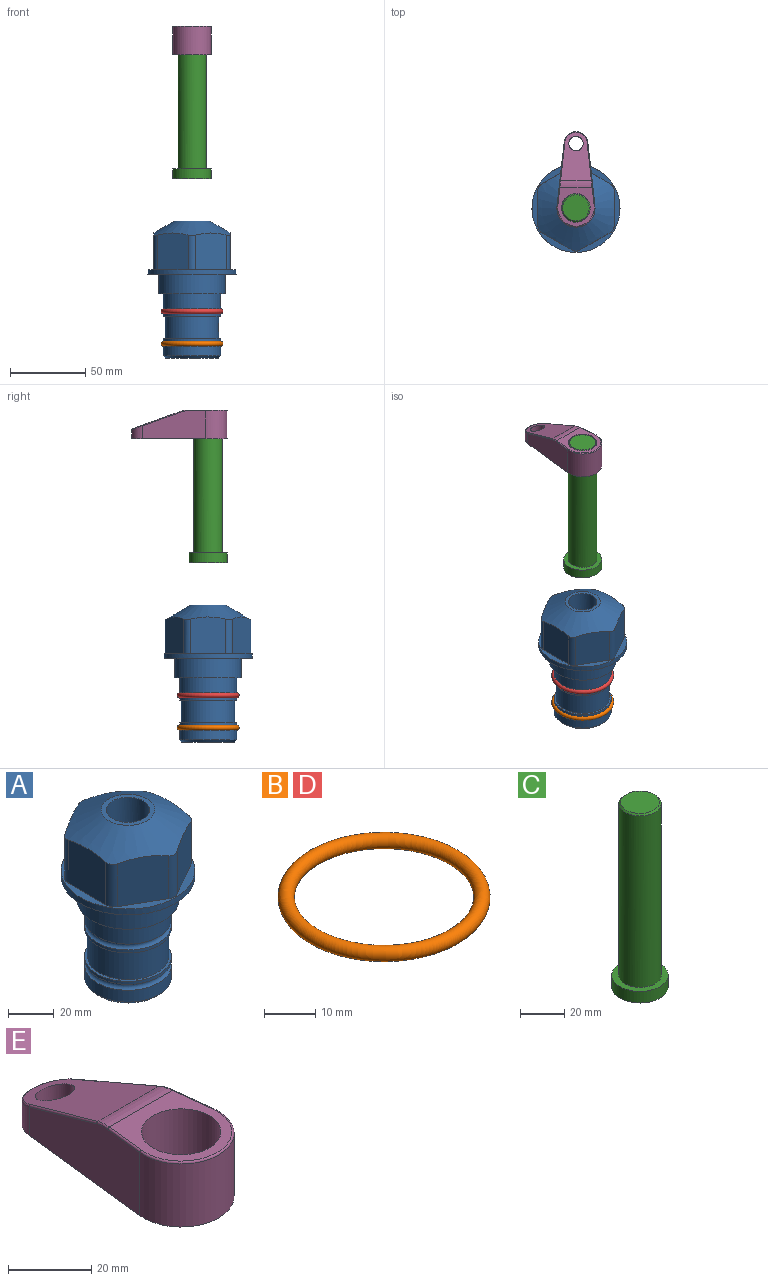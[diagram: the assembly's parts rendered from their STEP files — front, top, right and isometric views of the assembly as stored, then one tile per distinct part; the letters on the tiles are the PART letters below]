
ASSEMBLY  parts=5 mates=3
PART A: 36 faces, bbox 58.7x58.7x91.2 mm
  f0: cylinder r=17.78mm len=35.56mm, axis (0,0,1), area 1670.8mm2, adj f23,f24,f31
  f1: cylinder r=19.05mm len=38.1mm, axis (0,0,1), area 1191.9mm2, adj f26,f27,f30
  f2: plane 58.66x58.66mm, normal (0,0,-1), area 1150.6mm2, adj f3,f28
  f3: cylinder r=29.33mm len=58.66mm, axis (0,0,-1), area 585.1mm2, adj f2,f4
  f4: plane 58.66x58.66mm, normal (0,0,1), area 475.9mm2, adj f3,f5,f6,f7,f8,f9,f10,f11
  f5: plane 24.5x20.32mm, normal (-0.5,0.87,0), area 562.8mm2, adj f4,f15,f16,f17
  f6: plane 24.5x20.32mm, normal (0.5,0.87,0), area 562.8mm2, adj f4,f14,f15,f17
  f7: plane 24.5x23.48mm, normal (1,0,0), area 562.8mm2, adj f4,f13,f14,f17
  f8: plane 24.5x20.32mm, normal (0.5,-0.87,0), area 562.8mm2, adj f4,f12,f13,f17
  f9: plane 24.5x20.32mm, normal (-0.5,-0.87,0), area 562.8mm2, adj f4,f11,f12,f17
  f10: plane 24.5x23.48mm, normal (-1,0,0), area 562.8mm2, adj f4,f11,f16,f17
  f11: cylinder r=5.08mm len=23.01mm, axis (0,0,-1), area 121.2mm2, adj f4,f9,f10,f17
  f12: cylinder r=5.08mm len=23.01mm, axis (0,0,-1), area 121.2mm2, adj f4,f8,f9,f17
  f13: cylinder r=5.08mm len=23.01mm, axis (0,0,-1), area 121.2mm2, adj f4,f7,f8,f17
  f14: cylinder r=5.08mm len=23.01mm, axis (0,0,-1), area 121.2mm2, adj f4,f6,f7,f17
  f15: cylinder r=5.08mm len=23.01mm, axis (0,0,-1), area 121.2mm2, adj f4,f5,f6,f17
  f16: cylinder r=5.08mm len=23.01mm, axis (0,0,-1), area 121.2mm2, adj f4,f5,f10,f17
  f17: cone r=11.73mm half-angle=60deg, axis (0,0,-1), area 2071.8mm2, adj f5,f6,f7,f8,f9,f10,f11,f12
  f18: plane 23.46x23.46mm, normal (0,0,1), area 147.4mm2, adj f17,f35
  f19: plane 34.93x34.93mm, normal (0,0,-1), area 958mm2, adj f29
  f20: cylinder r=19.05mm len=38.1mm, axis (0,0,1), area 760.1mm2, adj f21,f29
  f21: torus R=19.05mm, axis (0,0,1), area 565.3mm2, adj f20,f22
  f22: cylinder r=19.05mm len=38.1mm, axis (0,0,1), area 190mm2, adj f21,f23
  f23: plane 38.1x38.1mm, normal (0,0,1), area 146.9mm2, adj f0,f22
  f24: plane 38.1x38.1mm, normal (0,0,-1), area 146.9mm2, adj f0,f25
  f25: cylinder r=19.05mm len=38.1mm, axis (0,0,1), area 190mm2, adj f24,f26
  f26: torus R=19.05mm, axis (0,0,1), area 565.3mm2, adj f1,f25
  f27: plane 44.45x44.45mm, normal (0,0,-1), area 411.7mm2, adj f1,f28
  f28: cylinder r=22.23mm len=44.45mm, axis (0,0,1), area 1773.5mm2, adj f2,f27
  f29: cone r=19.05mm half-angle=45deg, axis (0,0,1), area 257.5mm2, adj f19,f20
  f30: cylinder r=3.17mm len=6.75mm, axis (-1,0,0), area 128mm2, adj f1,f33
  f31: cylinder r=3.17mm len=6.35mm, axis (-1,0,0), area 102.5mm2, adj f0,f33
  f32: plane 25.4x25.4mm, normal (0,0,1), area 506.7mm2, adj f33
  f33: cylinder r=12.7mm len=66.42mm, axis (0,0,-1), area 5236.2mm2, adj f30,f31,f32,f34
  f34: cone r=9.53mm half-angle=30deg, axis (0,0,-1), area 443.4mm2, adj f33,f35
  f35: cylinder r=9.53mm len=19.05mm, axis (0,0,-1), area 849mm2, adj f18,f34
PART B: 1 faces, bbox 44.7x44.7x3.2 mm
  f0: torus R=19.05mm, axis (0,0,1), area 1193.9mm2
PART C: 6 faces, bbox 25.4x25.4x101.6 mm
  f0: plane 17.46x17.46mm, normal (0,0,1), area 239.5mm2, adj f5
  f1: plane 25.4x25.4mm, normal (0,0,-1), area 506.7mm2, adj f2
  f2: cylinder r=12.7mm len=25.4mm, axis (0,0,1), area 506.7mm2, adj f1,f3
  f3: plane 25.4x25.4mm, normal (0,0,1), area 221.7mm2, adj f2,f4
  f4: cylinder r=9.53mm len=94.46mm, axis (0,0,1), area 5653mm2, adj f3,f5
  f5: cone r=8.73mm half-angle=45deg, axis (0,0,-1), area 64.4mm2, adj f0,f4
PART D: same geometry as B
PART E: 44 faces, bbox 27.5x64.5x19.1 mm
  f0: plane 2.3x0.95mm, normal (0,0,-1), area 1mm2, adj f25,f30,f34
  f1: plane 63.5x25.4mm, normal (0,0,-1), area 561.7mm2, adj f2,f3,f4,f5,f6,f7,f19,f20
  f2: cylinder r=12.7mm len=25.4mm, axis (0,0,-1), area 792.2mm2, adj f1,f3,f5,f13
  f3: plane 42.33x18.54mm, normal (0.99,0.11,0), area 647mm2, adj f1,f2,f4,f11,f12,f14
  f4: cylinder r=7.94mm len=15.78mm, axis (0,0,-1), area 158.6mm2, adj f1,f3,f5,f16
  f5: plane 42.33x18.54mm, normal (-0.99,0.11,0), area 647mm2, adj f1,f2,f4,f15,f17,f18
  f6: cylinder r=9.53mm len=19.05mm, axis (0,0,-1), area 1140.1mm2, adj f1,f8
  f7: cylinder r=4.76mm len=10.98mm, axis (0,0,-1), area 276.1mm2, adj f1,f9
  f8: plane 25.83x24.38mm, normal (0,0,1), area 262.2mm2, adj f6,f10,f11,f13,f15
  f9: plane 32.49x20.55mm, normal (0,0.34,0.94), area 489.9mm2, adj f7,f10,f14,f16,f18
  f10: cylinder r=12.7mm len=21.49mm, axis (-1,0,0), area 93.2mm2, adj f8,f9,f12,f17
  f11: cylinder r=0.51mm len=12.34mm, axis (0.11,-0.99,0), area 9.9mm2, adj f3,f8,f12,f13
  f12: bspline ~7.62x1.64mm, area 3.5mm2, adj f3,f10,f11,f14
  f13: torus R=12.19mm, axis (0,0,1), area 33.6mm2, adj f2,f8,f11,f15
  f14: cylinder r=0.51mm len=26.01mm, axis (0.1,-0.93,0.34), area 21.6mm2, adj f3,f9,f12,f16
  f15: cylinder r=0.51mm len=12.34mm, axis (0.11,0.99,0), area 9.9mm2, adj f5,f8,f13,f17
  f16: bspline ~15.78x7.05mm, area 15.7mm2, adj f4,f9,f14,f18
  f17: bspline ~7.62x1.64mm, area 3.5mm2, adj f5,f10,f15,f18
  f18: cylinder r=0.51mm len=26.01mm, axis (0.1,0.93,-0.34), area 21.6mm2, adj f5,f9,f16,f17
  f19: plane 21.6x14.29mm, normal (-0.99,-0.11,0), area 242.6mm2, adj f1,f26,f28,f34,f36,f38
  f20: plane 21.6x14.29mm, normal (0.99,-0.11,0), area 242.6mm2, adj f1,f27,f29,f37,f39,f41
  f21: cylinder r=12.7mm len=14.29mm, axis (0,0,-1), area 173.2mm2, adj f1,f26,f27,f30,f31,f33
  f22: cylinder r=7.94mm len=7.63mm, axis (0,0,-1), area 53.8mm2, adj f1,f28,f29,f42
  f23: plane 2.3x0.95mm, normal (0,0,-1), area 1mm2, adj f25,f33,f37
  f24: plane 17.94x12.32mm, normal (0,-0.34,-0.94), area 191.2mm2, adj f25,f38,f41,f42
  f25: cylinder r=9.53mm len=12.93mm, axis (-1,0,0), area 37.5mm2, adj f0,f23,f24,f31,f36,f39
  f26: cylinder r=1.59mm len=14.29mm, axis (0,0,-1), area 49mm2, adj f1,f19,f21,f32
  f27: cylinder r=1.59mm len=14.29mm, axis (0,0,-1), area 49mm2, adj f1,f20,f21,f35
  f28: cylinder r=1.59mm len=7.28mm, axis (0,0,-1), area 22.1mm2, adj f1,f19,f22,f40
  f29: cylinder r=1.59mm len=7.28mm, axis (0,0,-1), area 22.1mm2, adj f1,f20,f22,f43
  f30: torus R=14.29mm, axis (0,0,1), area 5.8mm2, adj f0,f21,f31,f32
  f31: bspline ~11.06x2.73mm, area 20.8mm2, adj f21,f25,f30,f33
  f32: sphere r=1.59mm, area 5.4mm2, adj f26,f30,f34
  f33: torus R=14.29mm, axis (0,0,1), area 5.8mm2, adj f21,f23,f31,f35
  f34: cylinder r=1.59mm len=1.68mm, axis (-0.11,0.99,0), area 2.4mm2, adj f0,f19,f32,f36
  f35: sphere r=1.59mm, area 5.4mm2, adj f27,f33,f37
  f36: bspline ~5.82x2.33mm, area 7.7mm2, adj f19,f25,f34,f38
  f37: cylinder r=1.59mm len=1.68mm, axis (0.11,0.99,0), area 2.4mm2, adj f20,f23,f35,f39
  f38: cylinder r=1.59mm len=18.33mm, axis (0.1,-0.93,0.34), area 46.7mm2, adj f19,f24,f36,f40
  f39: bspline ~5.82x2.33mm, area 7.7mm2, adj f20,f25,f37,f41
  f40: sphere r=1.59mm, area 3.6mm2, adj f28,f38,f42
  f41: cylinder r=1.59mm len=18.33mm, axis (0.1,0.93,-0.34), area 46.7mm2, adj f20,f24,f39,f43
  f42: bspline ~8.31x1.84mm, area 15.3mm2, adj f22,f24,f40,f43
  f43: sphere r=1.59mm, area 3.6mm2, adj f29,f41,f42
PLACE A t=(-10.36,-32.93,0)mm fixed
PLACE B t=(-10.36,-32.93,-21.59)mm
PLACE C t=(-10.36,-32.93,91.86)mm
PLACE D t=(-10.36,-32.93,0)mm
PLACE E t=(-10.36,-32.93,146.47)mm
MATE fastened E.f2 <-> C.f2  axis (0,0,-1) through (-10.36,-32.93,165.52)mm
MATE cylindrical C.f2 <-> A.f0  axis (0,0,1) through (-10.36,-32.93,117.49)mm
MATE fastened B.f0 <-> A.f0  axis (0,0,1) through (-10.36,-32.93,-46.1)mm
